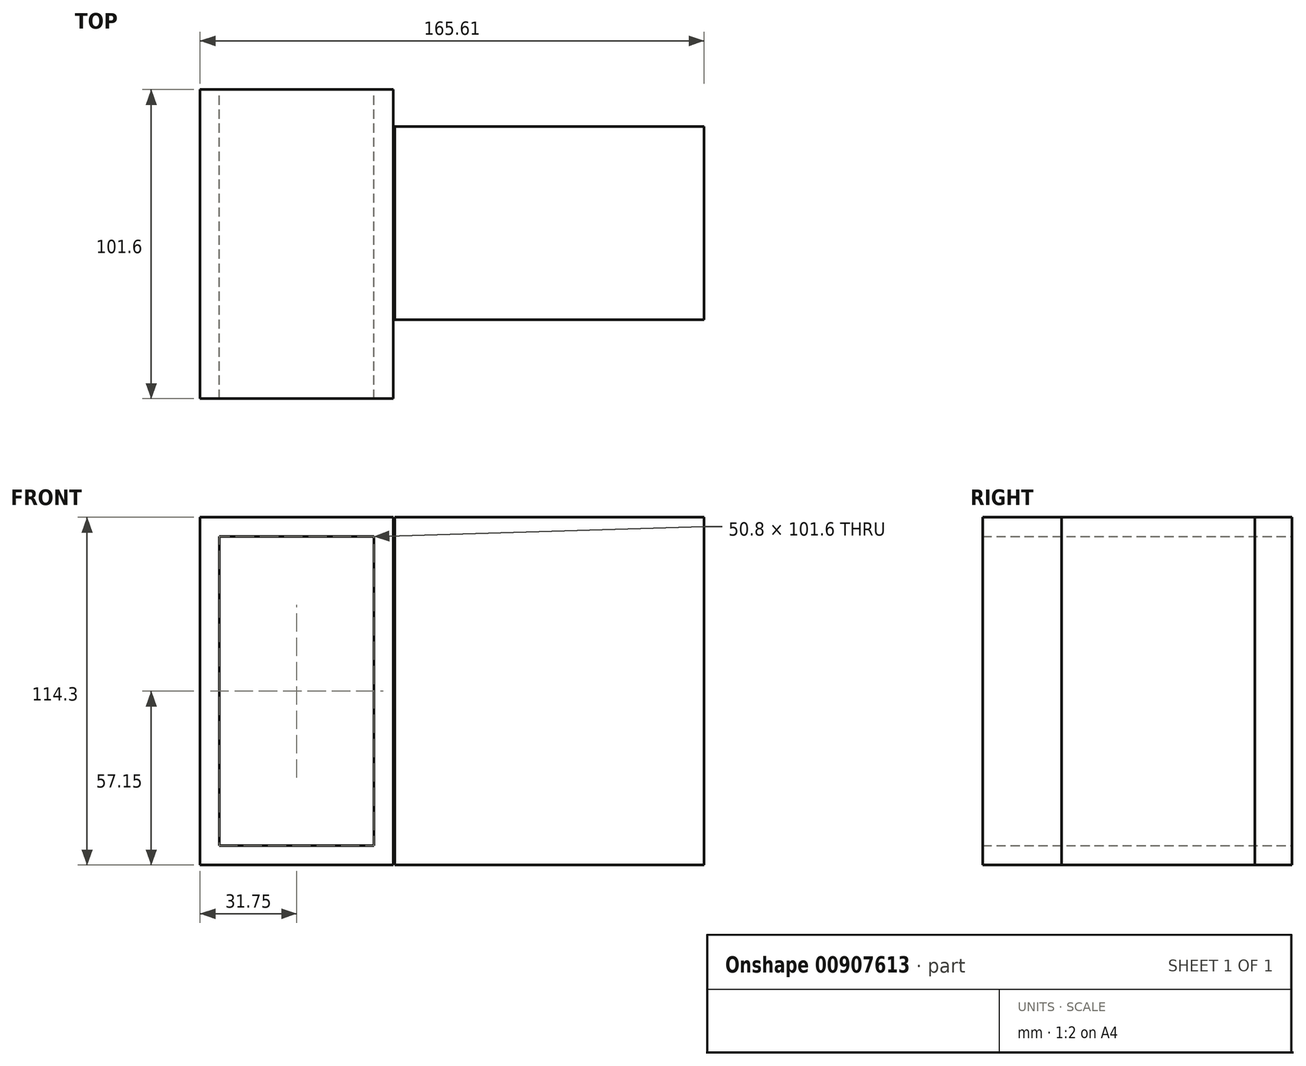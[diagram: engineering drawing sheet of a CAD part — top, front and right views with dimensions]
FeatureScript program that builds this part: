
annotation { "Feature Type Name" : "Feature", "Feature Type Description" : "" }
export const myFeature = defineFeature(function(context is Context, id is Id, definition is map)
    precondition{}
    {
        {
            var Q0;
            Q0=qCreatedBy(makeId("Front.planeOp"),FACE);
            var sketch = newSketch(context, id + "F0", { "sketchPlane" : qUnion([Q0])});
            skLineSegment(sketch, "E0.bottom", {"start": v(25.4, -50.8) * mm, "end": v(-25.4, -50.8) * mm});
            skLineSegment(sketch, "E0.top", {"start": v(25.4, 50.8) * mm, "end": v(-25.4, 50.8) * mm});
            skLineSegment(sketch, "E0.left", {"start": v(25.4, -50.8) * mm, "end": v(25.4, 50.8) * mm});
            skLineSegment(sketch, "E0.right", {"start": v(-25.4, -50.8) * mm, "end": v(-25.4, 50.8) * mm});
            skPoint(sketch, "E0.middle", {"position": v(0, 0) * mm});
            skLineSegment(sketch, "E1.bottom", {"start": v(31.75, -57.15) * mm, "end": v(-31.75, -57.15) * mm});
            skLineSegment(sketch, "E1.top", {"start": v(31.75, 57.15) * mm, "end": v(-31.75, 57.15) * mm});
            skLineSegment(sketch, "E1.left", {"start": v(31.75, -57.15) * mm, "end": v(31.75, 57.15) * mm});
            skLineSegment(sketch, "E1.right", {"start": v(-31.75, -57.15) * mm, "end": v(-31.75, 57.15) * mm});
            skSolve(sketch);
        }
        {
            var Q0;
            Q0 = qSketchRegion(id + "F0", true);
            extrude(context, id + "F1", {"entities" : qUnion([Q0]), "depth" : 101.6 * mm, "offsetDistance" : 25.4 * mm});
        }
        {
            var Q0;
            Q0=makeQuery(id+"F1.opExtrude","SWEPT_FACE",FACE,{"disambiguationData":[OSD([sQuery(id+"F0.wireOp",EDGE,"E1.left")])]});
            cPlane(context, id + "F2", {"entities" : qUnion([Q0]), "cplaneType" : CPlaneType.OFFSET, "offset" : 0.5 * mm, "width" : 152.4 * mm, "height" : 152.4 * mm});
        }
        {
            var Q0;
            Q0=qCreatedBy(id+"F2.planeOp",FACE);
            var sketch = newSketch(context, id + "F3", { "sketchPlane" : qUnion([Q0])});
            skLineSegment(sketch, "E2.bottom", {"start": v(-12.2, 57.15) * mm, "end": v(-75.7, 57.15) * mm});
            skLineSegment(sketch, "E2.top", {"start": v(-12.2, -57.15) * mm, "end": v(-75.7, -57.15) * mm});
            skLineSegment(sketch, "E2.left", {"start": v(-12.2, 57.15) * mm, "end": v(-12.2, -57.15) * mm});
            skLineSegment(sketch, "E2.right", {"start": v(-75.7, 57.15) * mm, "end": v(-75.7, -57.15) * mm});
            skPoint(sketch, "E2.middle", {"position": v(-43.94, 0) * mm});
            skSolve(sketch);
        }
        {
            var Q0;
            Q0=makeQuery(id+"F3.imprint","IMPRINT",FACE,{"disambiguationData":[TD([[makeQuery(id+"F3.imprint","IMPRINT",EDGE,{"derivedFrom":sQuery(id+"F3.wireOp",EDGE,"E2.bottom")}),1.0]])]});
            extrude(context, id + "F4", {"entities" : qUnion([Q0]), "depth" : 101.6 * mm, "offsetDistance" : 25.4 * mm});
        }
    });
